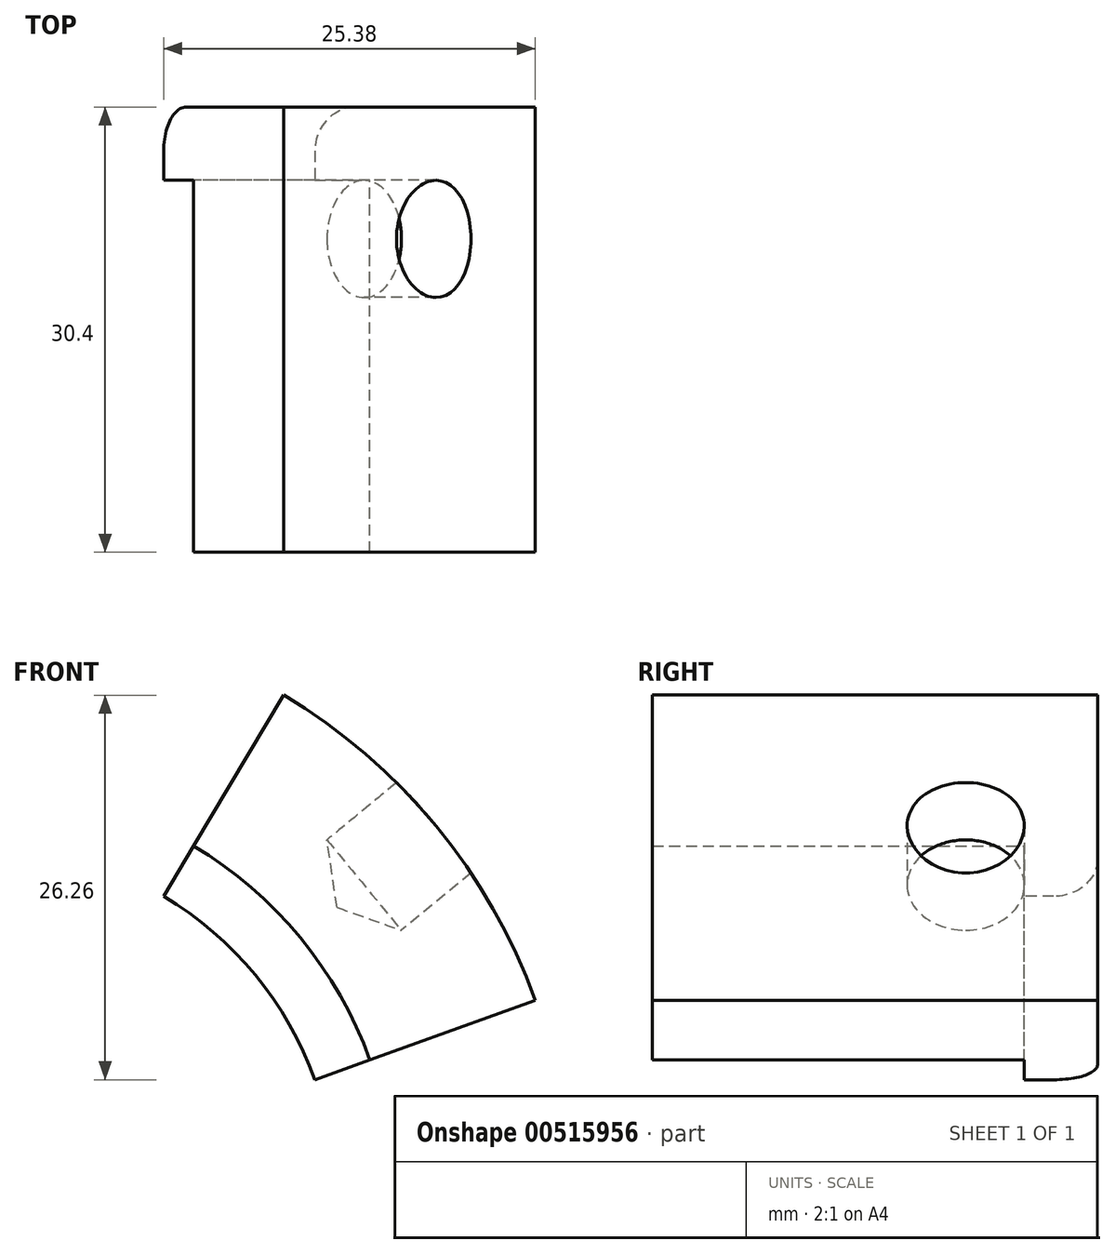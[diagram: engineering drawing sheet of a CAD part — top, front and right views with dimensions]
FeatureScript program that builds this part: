
annotation { "Feature Type Name" : "Feature", "Feature Type Description" : "" }
export const myFeature = defineFeature(function(context is Context, id is Id, definition is map)
    precondition{}
    {
        {
            var Q0;
            Q0=qCreatedBy(makeId("Front.planeOp"),FACE);
            var sketch = newSketch(context, id + "F0", { "sketchPlane" : qUnion([Q0])});
            skArc(sketch, "E0", {"start": v(37.65, 13.51) * mm, "mid": v(30.87, 25.44) * mm, "end": v(20.45, 34.37) * mm});
            skArc(sketch, "E1", {"start": v(26.35, 9.46) * mm, "mid": v(21.6, 17.8) * mm, "end": v(14.32, 24.06) * mm});
            skLineSegment(sketch, "E2", {"start": v(14.32, 24.06) * mm, "end": v(20.45, 34.37) * mm});
            skLineSegment(sketch, "E3", {"start": v(26.35, 9.46) * mm, "end": v(37.65, 13.51) * mm});
            skSolve(sketch);
        }
        {
            var Q0;
            Q0=qCreatedBy(makeId("Front.planeOp"),FACE);
            var sketch = newSketch(context, id + "F1", { "sketchPlane" : qUnion([Q0])});
            skArc(sketch, "E4", {"start": v(22.59, 8.1) * mm, "mid": v(18.52, 15.26) * mm, "end": v(12.27, 20.62) * mm});
            skLineSegment(sketch, "E5", {"start": v(20.5, 34.46) * mm, "end": v(12.27, 20.62) * mm});
            skLineSegment(sketch, "E6", {"start": v(37.65, 13.51) * mm, "end": v(22.59, 8.1) * mm});
            skArc(sketch, "E7", {"start": v(37.65, 13.51) * mm, "mid": v(30.87, 25.44) * mm, "end": v(20.45, 34.37) * mm});
            skSolve(sketch);
        }
        {
            var Q0;
            Q0=makeQuery(id+"F0.imprint","IMPRINT",FACE,{"disambiguationData":[TD([[makeQuery(id+"F0.imprint","IMPRINT",EDGE,{"derivedFrom":sQuery(id+"F0.wireOp",EDGE,"E0")}),1.0]])]});
            extrude(context, id + "F2", {"entities" : qUnion([Q0]), "depth" : 25.4 * mm, "offsetDistance" : 25 * mm});
        }
        {
            var Q0;
            Q0=qSketchRegion(id+"F1",true);
            var Q1;
            Q1=qSketchRegion(id+"F0",true);
            extrude(context, id + "F3", {"entities" : qUnion([Q0, Q1]), "operationType" : NewBodyOperationType.ADD, "oppositeDirection" : true, "depth" : 5 * mm, "offsetDistance" : 25 * mm});
        }
        {
            var Q0;
            Q0=makeQuery(id+"F2.opExtrude","CAP_VERTEX",VERTEX,{"disambiguationData":[OSD([sQuery(id+"F0.wireOp",EDGE,"E0"),sQuery(id+"F0.wireOp",EDGE,"E3")])],"isStart":false});
            var Q1;
            Q1=makeQuery(id+"F2.opExtrude","CAP_VERTEX",VERTEX,{"disambiguationData":[OSD([sQuery(id+"F0.wireOp",EDGE,"E0"),sQuery(id+"F0.wireOp",EDGE,"E2")])],"isStart":false});
            var Q2;
            Q2=sQuery(id+"F0.wireOp",VERTEX,"E2.end");
            cPlane(context, id + "F4", {"entities" : qUnion([Q0, Q1, Q2]), "cplaneType" : CPlaneType.THREE_POINT, "offset" : 0 * mm, "width" : 150 * mm, "height" : 150 * mm});
        }
        {
            var Q0;
            Q0=qCreatedBy(id+"F4.planeOp",FACE);
            var sketch = newSketch(context, id + "F5", { "sketchPlane" : qUnion([Q0])});
            skCircle(sketch, "E8", {"center": v(-4, 0) * mm, "radius": 2.5 * mm});
            skSolve(sketch);
        }
        {
            var Q0;
            Q0=sQuery(id+"F5.wireOp",VERTEX,"E8.center");
            var Q1;
            Q1=makeQuery(id+"F2.opExtrude","SWEPT_BODY",BODY,{"disambiguationData":[OSD([sQuery(id+"F0.wireOp",EDGE,"E0"),sQuery(id+"F0.wireOp",EDGE,"E1"),sQuery(id+"F0.wireOp",EDGE,"E2"),sQuery(id+"F0.wireOp",EDGE,"E3")])]});
            hole(context, id + "F6", {"style" : HoleStyle.SIMPLE, "endStyle" : HoleEndStyle.BLIND, "oppositeDirection" : true, "holeDiameter" : 8 * mm, "holeDepth" : 5 * mm, "isTappedThrough" : true, "tappedDepth" : 12 * mm, "tapClearance" : 3, "startFromSketch" : true, "locations" : qUnion([Q0]), "scope" : qUnion([Q1])});
        }
        {
            var Q0;
            Q0=sQuery(id+"F5.wireOp",VERTEX,"E8.center");
            var Q1;
            Q1=makeQuery(id+"F2.opExtrude","SWEPT_BODY",BODY,{"disambiguationData":[OSD([sQuery(id+"F0.wireOp",EDGE,"E0"),sQuery(id+"F0.wireOp",EDGE,"E1"),sQuery(id+"F0.wireOp",EDGE,"E2"),sQuery(id+"F0.wireOp",EDGE,"E3")])]});
            hole(context, id + "F7", {"style" : HoleStyle.SIMPLE, "endStyle" : HoleEndStyle.BLIND, "holeDiameter" : 8 * mm, "holeDepth" : 4 * mm, "isTappedThrough" : true, "tappedDepth" : 12 * mm, "tapClearance" : 3, "startFromSketch" : true, "locations" : qUnion([Q0]), "scope" : qUnion([Q1])});
        }
        {
            var Q0;
            Q0=makeQuery(id+"F3.opExtrude","CAP_EDGE",EDGE,{"disambiguationData":[OSD([sQuery(id+"F1.wireOp",EDGE,"E4")])],"isStart":false});
            fillet(context, id + "F8", {"entities" : qUnion([Q0]), "radius" : 3 * mm, "tangentPropagation" : true, "allowEdgeOverflow" : false});
        }
    });
